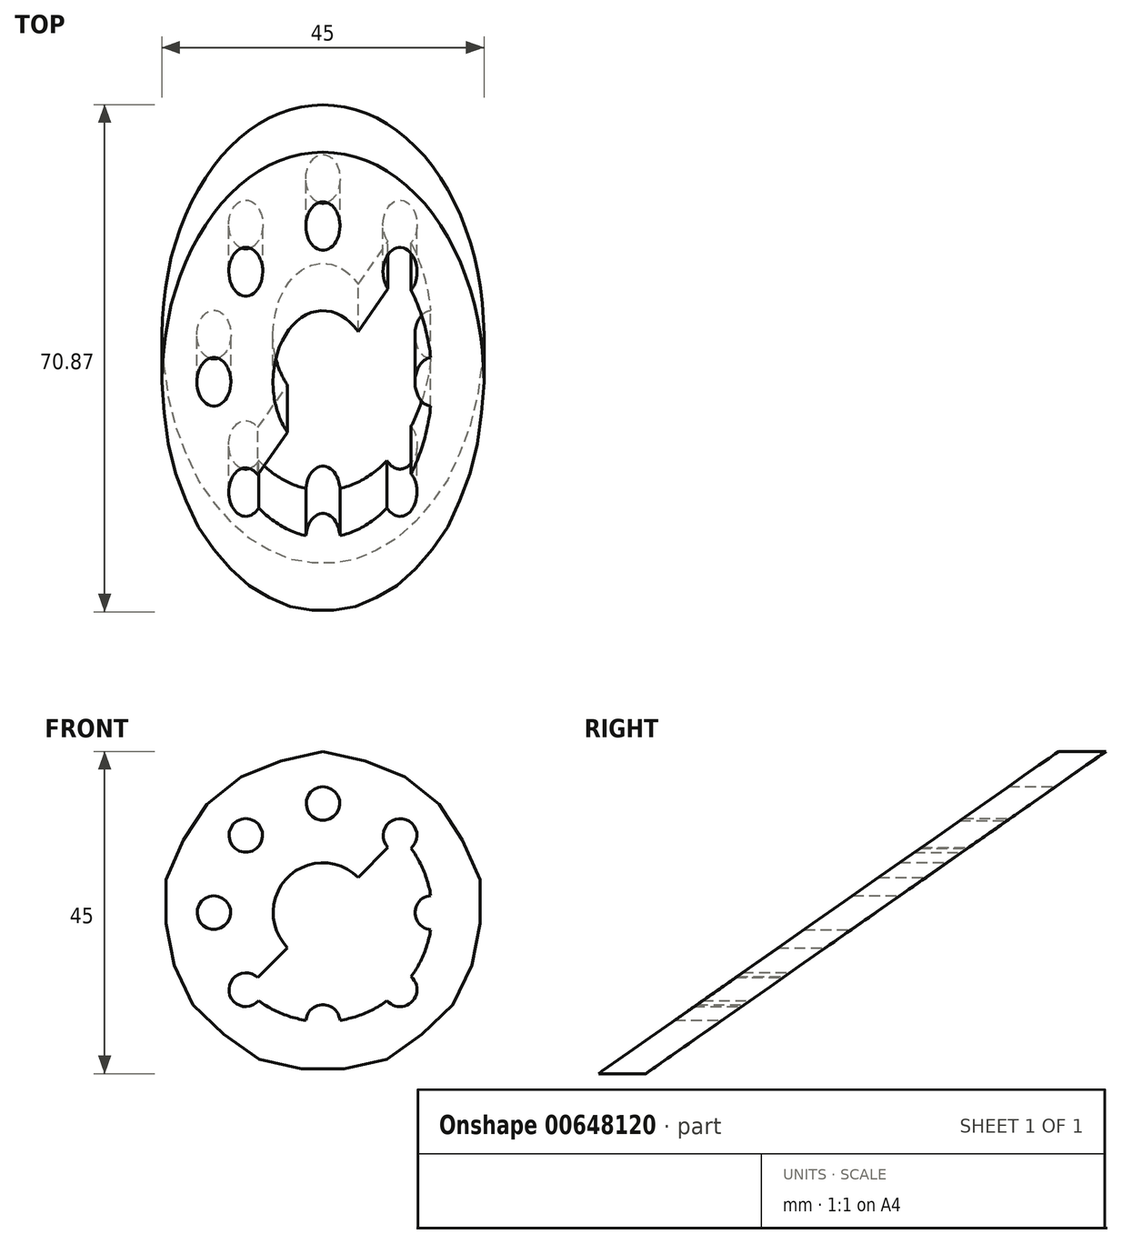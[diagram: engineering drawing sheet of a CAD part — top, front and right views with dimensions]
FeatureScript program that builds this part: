
annotation { "Feature Type Name" : "Feature", "Feature Type Description" : "" }
export const myFeature = defineFeature(function(context is Context, id is Id, definition is map)
    precondition{}
    {
        {
            var Q0;
            Q0=qCreatedBy(makeId("Front.planeOp"),FACE);
            var sketch = newSketch(context, id + "F0", { "sketchPlane" : qUnion([Q0])});
            skCircle(sketch, "E0", {"center": v(0, 0) * mm, "radius": 22.5 * mm});
            skSolve(sketch);
        }
        {
            var Q0;
            Q0 = qSketchRegion(id + "F0", true);
            extrude(context, id + "F1", {"entities" : qUnion([Q0]), "depth" : 101.6 * mm, "offsetDistance" : 25.4 * mm});
        }
        {
            var Q0;
            Q0=qCreatedBy(makeId("Right.planeOp"),FACE);
            var sketch = newSketch(context, id + "F2", { "sketchPlane" : qUnion([Q0])});
            skLineSegment(sketch, "E1", {"start": v(-79.78, -22.5) * mm, "end": v(-15.5, 22.5) * mm});
            skLineSegment(sketch, "E2", {"start": v(-76.48, -22.5) * mm, "end": v(-12.2, 22.5) * mm});
            skLineSegment(sketch, "E3", {"start": v(-83.08, -22.5) * mm, "end": v(-18.8, 22.5) * mm});
            skLineSegment(sketch, "E4", {"start": v(-79.78, -22.5) * mm, "end": v(-76.48, -22.5) * mm});
            skLineSegment(sketch, "E5", {"start": v(-12.2, 22.5) * mm, "end": v(-15.5, 22.5) * mm});
            skLineSegment(sketch, "E6", {"start": v(-18.8, 22.5) * mm, "end": v(-103.67, 26.25) * mm});
            skLineSegment(sketch, "E7", {"start": v(-103.67, 26.25) * mm, "end": v(-106.53, -38.46) * mm});
            skLineSegment(sketch, "E8", {"start": v(-106.53, -38.46) * mm, "end": v(-83.08, -22.5) * mm});
            skLineSegment(sketch, "E9", {"start": v(-76.48, -22.5) * mm, "end": v(27.35, -35.95) * mm});
            skLineSegment(sketch, "E10", {"start": v(27.35, -35.95) * mm, "end": v(27.35, 27.81) * mm});
            skLineSegment(sketch, "E11", {"start": v(27.35, 27.81) * mm, "end": v(-12.2, 22.5) * mm});
            skSolve(sketch);
        }
        {
            var Q0;
            Q0=makeQuery(id+"F2.imprint","IMPRINT",FACE,{"disambiguationData":[TD([[makeQuery(id+"F2.imprint","IMPRINT",EDGE,{"derivedFrom":sQuery(id+"F2.wireOp",EDGE,"E3")}),1.0]])]});
            extrude(context, id + "F3", {"entities" : qUnion([Q0]), "operationType" : NewBodyOperationType.REMOVE, "endBound" : BoundingType.THROUGH_ALL, "oppositeDirection" : true, "depth" : 25.4 * mm, "offsetDistance" : 25.4 * mm, "hasSecondDirection" : true, "secondDirectionBound" : SecondDirectionBoundingType.THROUGH_ALL, "secondDirectionOppositeDirection" : false, "secondDirectionDepth" : 25.4 * mm});
        }
        {
            var Q0;
            Q0=makeQuery(id+"F2.imprint","IMPRINT",FACE,{"disambiguationData":[TD([[makeQuery(id+"F2.imprint","IMPRINT",EDGE,{"derivedFrom":sQuery(id+"F2.wireOp",EDGE,"E2")}),-1.0]])]});
            extrude(context, id + "F4", {"entities" : qUnion([Q0]), "operationType" : NewBodyOperationType.REMOVE, "endBound" : BoundingType.THROUGH_ALL, "oppositeDirection" : true, "depth" : 25.4 * mm, "offsetDistance" : 25.4 * mm, "hasSecondDirection" : true, "secondDirectionBound" : SecondDirectionBoundingType.THROUGH_ALL, "secondDirectionOppositeDirection" : false, "secondDirectionDepth" : 25.4 * mm});
        }
        {
            var Q0;
            Q0=qCreatedBy(makeId("Front.planeOp"),FACE);
            var sketch = newSketch(context, id + "F5", { "sketchPlane" : qUnion([Q0])});
            skCircle(sketch, "E12", {"center": v(0, 0) * mm, "radius": 15.24 * mm});
            skCircle(sketch, "E13", {"center": v(0, 15.24) * mm, "radius": 2.38 * mm});
            skCircle(sketch, "E14", {"center": v(-15.24, 0) * mm, "radius": 2.38 * mm});
            skCircle(sketch, "E15", {"center": v(0, -15.24) * mm, "radius": 2.38 * mm});
            skCircle(sketch, "E16", {"center": v(15.24, 0) * mm, "radius": 2.38 * mm});
            skLineSegment(sketch, "E17", {"start": v(0, 0) * mm, "end": v(-21.26, 21.26) * mm});
            skLineSegment(sketch, "E18", {"start": v(0, 0) * mm, "end": v(25.83, -25.83) * mm});
            skLineSegment(sketch, "E19", {"start": v(0, 0) * mm, "end": v(20.37, 20.37) * mm});
            skLineSegment(sketch, "E20", {"start": v(0, 0) * mm, "end": v(-27.17, -27.17) * mm});
            skLineSegment(sketch, "E21", {"start": v(0, 0) * mm, "end": v(-15.24, 0) * mm});
            skCircle(sketch, "E22", {"center": v(10.78, 10.78) * mm, "radius": 2.38 * mm});
            skCircle(sketch, "E23", {"center": v(-10.78, 10.78) * mm, "radius": 2.38 * mm});
            skCircle(sketch, "E24", {"center": v(-10.78, -10.78) * mm, "radius": 2.38 * mm});
            skCircle(sketch, "E25", {"center": v(10.78, -10.78) * mm, "radius": 2.38 * mm});
            skSolve(sketch);
        }
        {
            var Q0;
            {var subQ0=sQuery(id+"F5.wireOp",EDGE,"E25");var subQ1=sQuery(id+"F5.wireOp",EDGE,"E12");var subQ2=makeQuery(id+"F5.imprint","INTERSECT",VERTEX,{"disambiguationData":[OD(0.0)],"derivedFrom":[subQ1,subQ0]});Q0=makeQuery(id+"F5.imprint","IMPRINT",FACE,{"disambiguationData":[TD([[makeQuery(id+"F5.imprint","IMPRINT",EDGE,{"disambiguationData":[TD([[subQ2,-1.0]])],"derivedFrom":subQ1}),1.0]])]});}
            var Q1;
            {var subQ0=sQuery(id+"F5.wireOp",EDGE,"E25");var subQ1=sQuery(id+"F5.wireOp",EDGE,"E12");var subQ2=makeQuery(id+"F5.imprint","INTERSECT",VERTEX,{"disambiguationData":[OD(1.0)],"derivedFrom":[subQ1,subQ0]});Q1=makeQuery(id+"F5.imprint","IMPRINT",FACE,{"disambiguationData":[TD([[makeQuery(id+"F5.imprint","IMPRINT",EDGE,{"disambiguationData":[TD([[subQ2,1.0]])],"derivedFrom":subQ1}),1.0]])]});}
            var Q2;
            {var subQ0=sQuery(id+"F5.wireOp",EDGE,"E25");var subQ1=sQuery(id+"F5.wireOp",EDGE,"E12");var subQ2=makeQuery(id+"F5.imprint","INTERSECT",VERTEX,{"disambiguationData":[OD(0.0)],"derivedFrom":[subQ1,subQ0]});Q2=makeQuery(id+"F5.imprint","IMPRINT",FACE,{"disambiguationData":[TD([[makeQuery(id+"F5.imprint","IMPRINT",EDGE,{"disambiguationData":[TD([[subQ2,-1.0]])],"derivedFrom":subQ1}),-1.0]])]});}
            var Q3;
            {var subQ0=sQuery(id+"F5.wireOp",EDGE,"E16");var subQ1=sQuery(id+"F5.wireOp",EDGE,"E12");var subQ2=makeQuery(id+"F5.imprint","INTERSECT",VERTEX,{"disambiguationData":[OD(0.0)],"derivedFrom":[subQ1,subQ0]});Q3=makeQuery(id+"F5.imprint","IMPRINT",FACE,{"disambiguationData":[TD([[makeQuery(id+"F5.imprint","IMPRINT",EDGE,{"disambiguationData":[TD([[subQ2,1.0]])],"derivedFrom":subQ1}),1.0]])]});}
            var Q4;
            {var subQ0=sQuery(id+"F5.wireOp",EDGE,"E16");var subQ1=sQuery(id+"F5.wireOp",EDGE,"E12");var subQ2=makeQuery(id+"F5.imprint","INTERSECT",VERTEX,{"disambiguationData":[OD(0.0)],"derivedFrom":[subQ1,subQ0]});Q4=makeQuery(id+"F5.imprint","IMPRINT",FACE,{"disambiguationData":[TD([[makeQuery(id+"F5.imprint","IMPRINT",EDGE,{"disambiguationData":[TD([[subQ2,1.0]])],"derivedFrom":subQ1}),-1.0]])]});}
            var Q5;
            {var subQ0=sQuery(id+"F5.wireOp",EDGE,"E13");var subQ1=sQuery(id+"F5.wireOp",EDGE,"E12");var subQ2=makeQuery(id+"F5.imprint","INTERSECT",VERTEX,{"disambiguationData":[OD(0.0)],"derivedFrom":[subQ1,subQ0]});Q5=makeQuery(id+"F5.imprint","IMPRINT",FACE,{"disambiguationData":[TD([[makeQuery(id+"F5.imprint","IMPRINT",EDGE,{"disambiguationData":[TD([[subQ2,-1.0]])],"derivedFrom":subQ1}),-1.0]])]});}
            var Q6;
            {var subQ0=sQuery(id+"F5.wireOp",EDGE,"E13");var subQ1=sQuery(id+"F5.wireOp",EDGE,"E12");var subQ2=makeQuery(id+"F5.imprint","INTERSECT",VERTEX,{"disambiguationData":[OD(0.0)],"derivedFrom":[subQ1,subQ0]});Q6=makeQuery(id+"F5.imprint","IMPRINT",FACE,{"disambiguationData":[TD([[makeQuery(id+"F5.imprint","IMPRINT",EDGE,{"disambiguationData":[TD([[subQ2,-1.0]])],"derivedFrom":subQ1}),1.0]])]});}
            var Q7;
            {var subQ0=sQuery(id+"F5.wireOp",EDGE,"E15");var subQ1=sQuery(id+"F5.wireOp",EDGE,"E12");var subQ2=makeQuery(id+"F5.imprint","INTERSECT",VERTEX,{"disambiguationData":[OD(0.0)],"derivedFrom":[subQ1,subQ0]});Q7=makeQuery(id+"F5.imprint","IMPRINT",FACE,{"disambiguationData":[TD([[makeQuery(id+"F5.imprint","IMPRINT",EDGE,{"disambiguationData":[TD([[subQ2,-1.0]])],"derivedFrom":subQ1}),-1.0]])]});}
            var Q8;
            {var subQ0=sQuery(id+"F5.wireOp",EDGE,"E23");var subQ1=sQuery(id+"F5.wireOp",EDGE,"E12");var subQ2=makeQuery(id+"F5.imprint","INTERSECT",VERTEX,{"disambiguationData":[OD(1.0)],"derivedFrom":[subQ1,subQ0]});Q8=makeQuery(id+"F5.imprint","IMPRINT",FACE,{"disambiguationData":[TD([[makeQuery(id+"F5.imprint","IMPRINT",EDGE,{"disambiguationData":[TD([[subQ2,1.0]])],"derivedFrom":subQ1}),1.0]])]});}
            var Q9;
            {var subQ0=sQuery(id+"F5.wireOp",EDGE,"E23");var subQ1=sQuery(id+"F5.wireOp",EDGE,"E12");var subQ2=makeQuery(id+"F5.imprint","INTERSECT",VERTEX,{"disambiguationData":[OD(1.0)],"derivedFrom":[subQ1,subQ0]});Q9=makeQuery(id+"F5.imprint","IMPRINT",FACE,{"disambiguationData":[TD([[makeQuery(id+"F5.imprint","IMPRINT",EDGE,{"disambiguationData":[TD([[subQ2,1.0]])],"derivedFrom":subQ1}),-1.0]])]});}
            var Q10;
            {var subQ0=sQuery(id+"F5.wireOp",EDGE,"E24");var subQ1=sQuery(id+"F5.wireOp",EDGE,"E12");var subQ2=makeQuery(id+"F5.imprint","INTERSECT",VERTEX,{"disambiguationData":[OD(1.0)],"derivedFrom":[subQ1,subQ0]});Q10=makeQuery(id+"F5.imprint","IMPRINT",FACE,{"disambiguationData":[TD([[makeQuery(id+"F5.imprint","IMPRINT",EDGE,{"disambiguationData":[TD([[subQ2,1.0]])],"derivedFrom":subQ1}),1.0]])]});}
            var Q11;
            {var subQ0=sQuery(id+"F5.wireOp",EDGE,"E12");var subQ1=makeQuery(id+"F5.imprint","INTERSECT",VERTEX,{"derivedFrom":[subQ0,sQuery(id+"F5.wireOp",EDGE,"E21")]});Q11=makeQuery(id+"F5.imprint","IMPRINT",FACE,{"disambiguationData":[TD([[makeQuery(id+"F5.imprint","IMPRINT",EDGE,{"disambiguationData":[TD([[subQ1,1.0]])],"derivedFrom":subQ0}),-1.0]])]});}
            var Q12;
            {var subQ0=sQuery(id+"F5.wireOp",EDGE,"E22");var subQ1=sQuery(id+"F5.wireOp",EDGE,"E12");var subQ2=makeQuery(id+"F5.imprint","INTERSECT",VERTEX,{"disambiguationData":[OD(0.0)],"derivedFrom":[subQ1,subQ0]});Q12=makeQuery(id+"F5.imprint","IMPRINT",FACE,{"disambiguationData":[TD([[makeQuery(id+"F5.imprint","IMPRINT",EDGE,{"disambiguationData":[TD([[subQ2,-1.0]])],"derivedFrom":subQ1}),1.0]])]});}
            var Q13;
            {var subQ0=sQuery(id+"F5.wireOp",EDGE,"E21");var subQ1=sQuery(id+"F5.wireOp",EDGE,"E12");var subQ2=makeQuery(id+"F5.imprint","INTERSECT",VERTEX,{"derivedFrom":[subQ1,subQ0]});Q13=makeQuery(id+"F5.imprint","IMPRINT",FACE,{"disambiguationData":[TD([[makeQuery(id+"F5.imprint","IMPRINT",EDGE,{"disambiguationData":[TD([[subQ2,-1.0]])],"derivedFrom":subQ1}),1.0]])]});}
            var Q14;
            {var subQ0=sQuery(id+"F5.wireOp",EDGE,"E21");var subQ1=sQuery(id+"F5.wireOp",EDGE,"E12");var subQ2=makeQuery(id+"F5.imprint","INTERSECT",VERTEX,{"derivedFrom":[subQ1,subQ0]});Q14=makeQuery(id+"F5.imprint","IMPRINT",FACE,{"disambiguationData":[TD([[makeQuery(id+"F5.imprint","IMPRINT",EDGE,{"disambiguationData":[TD([[subQ2,1.0]])],"derivedFrom":subQ1}),1.0]])]});}
            var Q15;
            {var subQ0=sQuery(id+"F5.wireOp",EDGE,"E23");var subQ1=sQuery(id+"F5.wireOp",EDGE,"E12");var subQ2=makeQuery(id+"F5.imprint","INTERSECT",VERTEX,{"disambiguationData":[OD(0.0)],"derivedFrom":[subQ1,subQ0]});Q15=makeQuery(id+"F5.imprint","IMPRINT",FACE,{"disambiguationData":[TD([[makeQuery(id+"F5.imprint","IMPRINT",EDGE,{"disambiguationData":[TD([[subQ2,-1.0]])],"derivedFrom":subQ1}),1.0]])]});}
            var Q16;
            {var subQ0=sQuery(id+"F5.wireOp",EDGE,"E22");var subQ1=sQuery(id+"F5.wireOp",EDGE,"E12");var subQ2=makeQuery(id+"F5.imprint","INTERSECT",VERTEX,{"disambiguationData":[OD(1.0)],"derivedFrom":[subQ1,subQ0]});Q16=makeQuery(id+"F5.imprint","IMPRINT",FACE,{"disambiguationData":[TD([[makeQuery(id+"F5.imprint","IMPRINT",EDGE,{"disambiguationData":[TD([[subQ2,1.0]])],"derivedFrom":subQ1}),1.0]])]});}
            var Q17;
            {var subQ0=sQuery(id+"F5.wireOp",EDGE,"E15");var subQ1=sQuery(id+"F5.wireOp",EDGE,"E12");var subQ2=makeQuery(id+"F5.imprint","INTERSECT",VERTEX,{"disambiguationData":[OD(0.0)],"derivedFrom":[subQ1,subQ0]});Q17=makeQuery(id+"F5.imprint","IMPRINT",FACE,{"disambiguationData":[TD([[makeQuery(id+"F5.imprint","IMPRINT",EDGE,{"disambiguationData":[TD([[subQ2,-1.0]])],"derivedFrom":subQ1}),1.0]])]});}
            extrude(context, id + "F6", {"entities" : qUnion([Q0, Q1, Q2, Q3, Q4, Q5, Q6, Q7, Q8, Q9, Q10, Q11, Q12, Q13, Q14, Q15, Q16, Q17]), "operationType" : NewBodyOperationType.REMOVE, "endBound" : BoundingType.THROUGH_ALL, "depth" : 25.4 * mm, "offsetDistance" : 25.4 * mm});
        }
        {
            var Q0;
            Q0=qCreatedBy(makeId("Front.planeOp"),FACE);
            var sketch = newSketch(context, id + "F7", { "sketchPlane" : qUnion([Q0])});
            skCircle(sketch, "E26", {"center": v(10.78, 10.78) * mm, "radius": 2.38 * mm});
            skSolve(sketch);
        }
        {
            var Q0;
            Q0 = qSketchRegion(id + "F7", true);
            extrude(context, id + "F8", {"entities" : qUnion([Q0]), "operationType" : NewBodyOperationType.REMOVE, "endBound" : BoundingType.THROUGH_ALL, "depth" : 25.4 * mm, "offsetDistance" : 25.4 * mm});
        }
        {
            var Q0;
            Q0=qCreatedBy(makeId("Front.planeOp"),FACE);
            var sketch = newSketch(context, id + "F9", { "sketchPlane" : qUnion([Q0])});
            skCircle(sketch, "E27", {"center": v(10.78, -10.78) * mm, "radius": 2.38 * mm});
            skCircle(sketch, "E28", {"center": v(-10.78, -10.78) * mm, "radius": 2.38 * mm});
            skCircle(sketch, "E29", {"center": v(-10.78, 10.78) * mm, "radius": 2.38 * mm});
            skCircle(sketch, "E30", {"center": v(0, 0) * mm, "radius": 6.99 * mm});
            skSolve(sketch);
        }
        {
            var Q0;
            Q0 = qSketchRegion(id + "F9", true);
            extrude(context, id + "F10", {"entities" : qUnion([Q0]), "operationType" : NewBodyOperationType.REMOVE, "endBound" : BoundingType.THROUGH_ALL, "depth" : 25.4 * mm, "offsetDistance" : 25.4 * mm});
        }
    });
